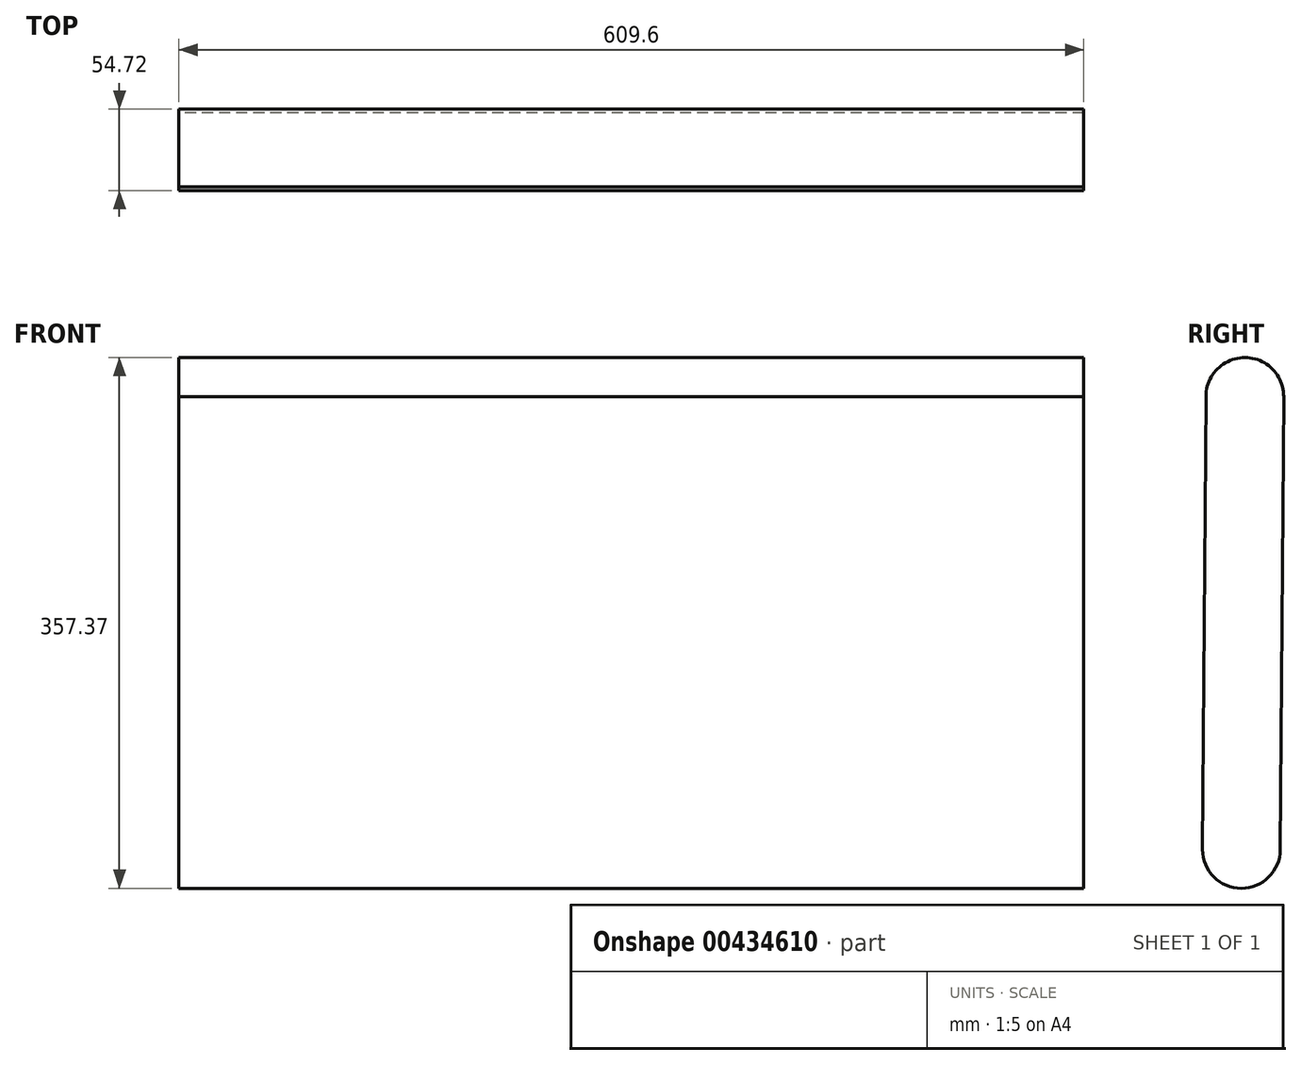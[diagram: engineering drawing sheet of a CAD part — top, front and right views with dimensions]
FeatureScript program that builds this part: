
annotation { "Feature Type Name" : "Feature", "Feature Type Description" : "" }
export const myFeature = defineFeature(function(context is Context, id is Id, definition is map)
    precondition{}
    {
        {
            var Q0;
            Q0=qCreatedBy(makeId("Right.planeOp"),FACE);
            var sketch = newSketch(context, id + "F0", { "sketchPlane" : qUnion([Q0])});
            skCircle(sketch, "E0", {"center": v(-5.49, 47.9) * mm, "radius": 26.19 * mm});
            skCircle(sketch, "E1", {"center": v(-7.83, -257.1) * mm, "radius": 26.19 * mm});
            skLineSegment(sketch, "E2", {"start": v(18.36, -257.1) * mm, "end": v(20.7, 47.7) * mm});
            skLineSegment(sketch, "E3", {"start": v(-34.02, -257.1) * mm, "end": v(-31.68, 47.82) * mm});
            skSolve(sketch);
        }
        {
            var Q0;
            {var subQ0=sQuery(id+"F0.wireOp",EDGE,"E2");Q0=makeQuery(id+"F0.imprint","IMPRINT",FACE,{"disambiguationData":[TD([[makeQuery(id+"F0.imprint","IMPRINT",EDGE,{"derivedFrom":subQ0}),1.0]])]});}
            var Q1;
            {var subQ0=sQuery(id+"F0.wireOp",EDGE,"E1");var subQ1=makeQuery(id+"F0.imprint","INTERSECT",VERTEX,{"derivedFrom":[subQ0,sQuery(id+"F0.wireOp",EDGE,"E2")]});Q1=makeQuery(id+"F0.imprint","IMPRINT",FACE,{"disambiguationData":[TD([[makeQuery(id+"F0.imprint","IMPRINT",EDGE,{"disambiguationData":[TD([[subQ1,-1.0]])],"derivedFrom":subQ0}),1.0]])]});}
            var Q2;
            {var subQ0=sQuery(id+"F0.wireOp",EDGE,"E0");var subQ1=makeQuery(id+"F0.imprint","INTERSECT",VERTEX,{"derivedFrom":[subQ0,sQuery(id+"F0.wireOp",EDGE,"E2")]});Q2=makeQuery(id+"F0.imprint","IMPRINT",FACE,{"disambiguationData":[TD([[makeQuery(id+"F0.imprint","IMPRINT",EDGE,{"disambiguationData":[TD([[subQ1,1.0]])],"derivedFrom":subQ0}),1.0]])]});}
            extrude(context, id + "F1", {"entities" : qUnion([Q0, Q1, Q2]), "depth" : 609.6 * mm});
        }
    });
